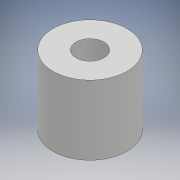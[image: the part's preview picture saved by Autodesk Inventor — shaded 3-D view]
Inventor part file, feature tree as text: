
AUTODESK INVENTOR PART (.ipt)
format: ipt  version: 2018 (Build 220112000, 112)  size: 92,672 bytes
history: native  units: mm
features: extrude x1, sketch x1
ambient origin geometry x8: Origin, YZ Plane, XZ Plane, XY Plane, X Axis, Y Axis, Z Axis, Center Point
bodies: Solid1 (feature_tree)
feature tree (2):
  extrude  "Extrusion1"  Depth=10.0mm
  sketch  "Sketch1"  dims[d0=12.0mm d1=10.0mm d2=30.0mm d3=0.0mm]
